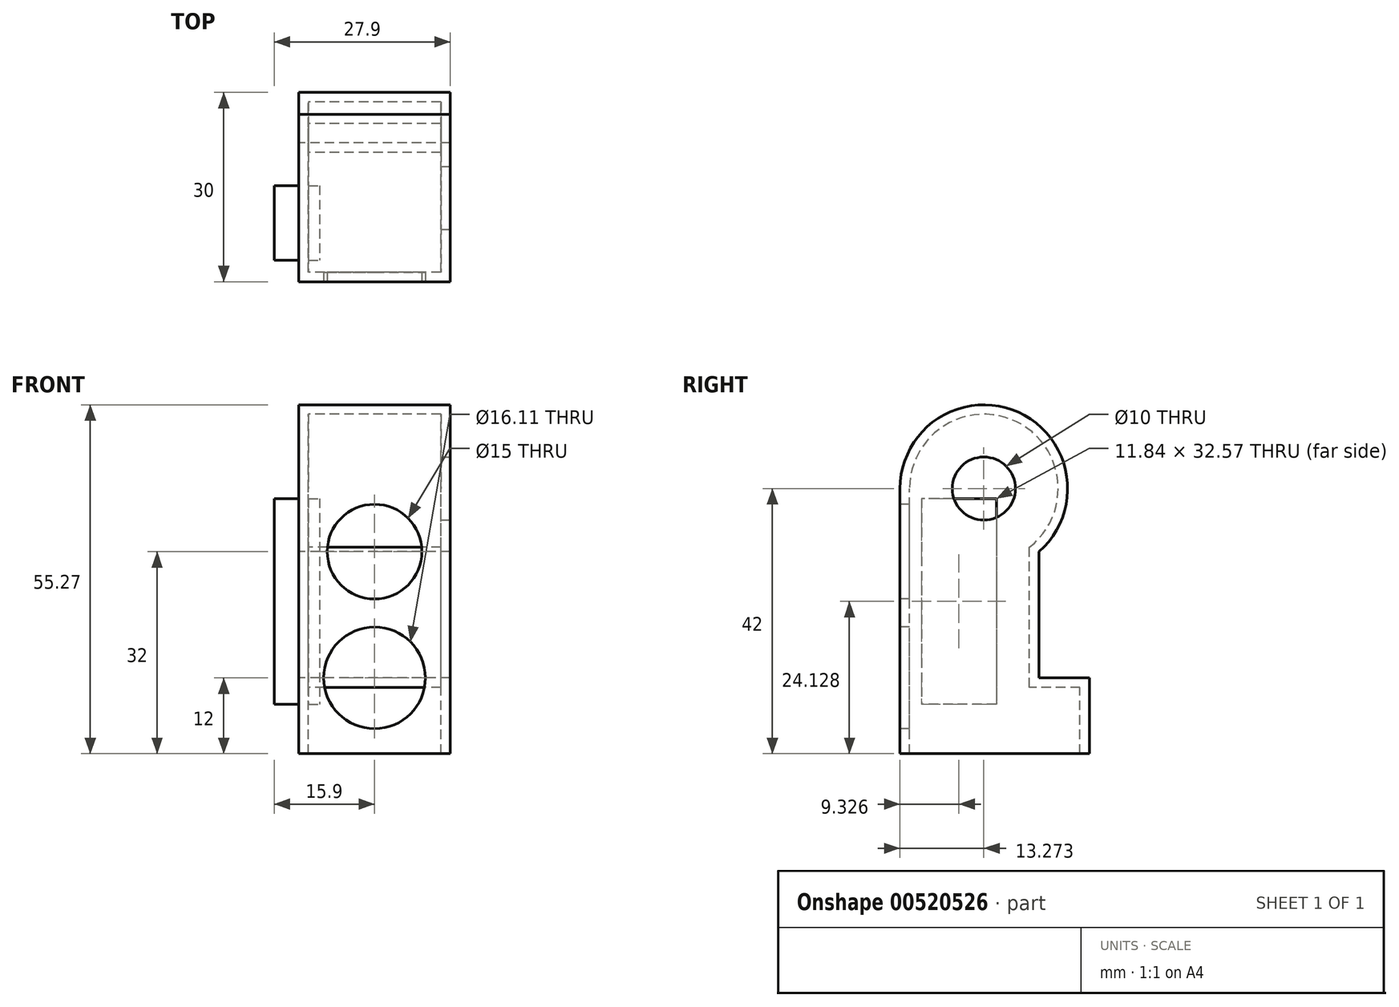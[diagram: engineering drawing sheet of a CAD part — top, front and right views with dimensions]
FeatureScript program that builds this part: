
annotation { "Feature Type Name" : "Feature", "Feature Type Description" : "" }
export const myFeature = defineFeature(function(context is Context, id is Id, definition is map)
    precondition{}
    {
        {
            var Q0;
            Q0=qCreatedBy(makeId("Right.planeOp"),FACE);
            var sketch = newSketch(context, id + "F0", { "sketchPlane" : qUnion([Q0])});
            skLineSegment(sketch, "E0", {"start": v(0, 0) * mm, "end": v(0, 42) * mm});
            skLineSegment(sketch, "E1", {"start": v(0, 0) * mm, "end": v(30, 0) * mm});
            skLineSegment(sketch, "E2", {"start": v(30, 0) * mm, "end": v(30, 12) * mm});
            skLineSegment(sketch, "E3", {"start": v(30, 12) * mm, "end": v(22, 12) * mm});
            skLineSegment(sketch, "E4", {"start": v(22, 12) * mm, "end": v(22, 32) * mm});
            skArc(sketch, "E5", {"start": v(22, 32) * mm, "mid": v(18.77, 54.08) * mm, "end": v(0, 42) * mm});
            skSolve(sketch);
        }
        {
            var Q0;
            Q0=makeQuery(id+"F0.imprint","IMPRINT",FACE,{"disambiguationData":[TD([[makeQuery(id+"F0.imprint","IMPRINT",EDGE,{"derivedFrom":sQuery(id+"F0.wireOp",EDGE,"E0")}),-1.0]])]});
            extrude(context, id + "F1", {"entities" : qUnion([Q0]), "endBound" : BoundingType.SYMMETRIC, "depth" : 24 * mm});
        }
        {
            var Q0;
            Q0=makeQuery(id+"F1.opExtrude","SWEPT_FACE",FACE,{"disambiguationData":[OSD([sQuery(id+"F0.wireOp",EDGE,"E1")])]});
            shell(context, id + "F2", {"entities" : qUnion([Q0]), "thickness" : 1.5 * mm});
        }
        {
            var Q0;
            Q0=makeQuery(id+"F1.opExtrude","CAP_FACE",FACE,{"disambiguationData":[OSD([sQuery(id+"F0.wireOp",EDGE,"E0"),sQuery(id+"F0.wireOp",EDGE,"E1"),sQuery(id+"F0.wireOp",EDGE,"E2"),sQuery(id+"F0.wireOp",EDGE,"E3"),sQuery(id+"F0.wireOp",EDGE,"E4"),sQuery(id+"F0.wireOp",EDGE,"E5")])],"isStart":false});
            var sketch = newSketch(context, id + "F3", { "sketchPlane" : qUnion([Q0])});
            skCircle(sketch, "E6", {"center": v(13.27, 42) * mm, "radius": 5 * mm});
            skSolve(sketch);
        }
        {
            var Q0;
            Q0=qSketchRegion(id+"F3",true);
            extrude(context, id + "F4", {"entities" : qUnion([Q0]), "operationType" : NewBodyOperationType.REMOVE, "oppositeDirection" : true, "depth" : 5 * mm});
        }
        {
            var Q0;
            Q0=makeQuery(id+"F1.opExtrude","SWEPT_FACE",FACE,{"disambiguationData":[OSD([sQuery(id+"F0.wireOp",EDGE,"E0")])]});
            var sketch = newSketch(context, id + "F5", { "sketchPlane" : qUnion([Q0])});
            skCircle(sketch, "E7", {"center": v(0, 12) * mm, "radius": 8.05 * mm});
            skCircle(sketch, "E8", {"center": v(0, 32) * mm, "radius": 7.5 * mm});
            skSolve(sketch);
        }
        {
            var Q0;
            Q0=makeQuery(id+"F5.imprint","IMPRINT",FACE,{"disambiguationData":[TD([[makeQuery(id+"F5.imprint","IMPRINT",EDGE,{"derivedFrom":sQuery(id+"F5.wireOp",EDGE,"E8")}),1.0]])]});
            var Q1;
            Q1=makeQuery(id+"F5.imprint","IMPRINT",FACE,{"disambiguationData":[TD([[makeQuery(id+"F5.imprint","IMPRINT",EDGE,{"derivedFrom":sQuery(id+"F5.wireOp",EDGE,"E7")}),1.0]])]});
            extrude(context, id + "F6", {"entities" : qUnion([Q0, Q1]), "operationType" : NewBodyOperationType.REMOVE, "oppositeDirection" : true, "depth" : 5 * mm});
        }
        {
            var Q0;
            Q0=makeQuery(id+"F1.opExtrude","SWEPT_BODY",BODY,{"disambiguationData":[OSD([sQuery(id+"F0.wireOp",EDGE,"E0"),sQuery(id+"F0.wireOp",EDGE,"E1"),sQuery(id+"F0.wireOp",EDGE,"E2"),sQuery(id+"F0.wireOp",EDGE,"E3"),sQuery(id+"F0.wireOp",EDGE,"E4"),sQuery(id+"F0.wireOp",EDGE,"E5")])]});
            var Q1;
            Q1=makeQuery(id+"F1.opExtrude","CAP_FACE",FACE,{"disambiguationData":[OSD([sQuery(id+"F0.wireOp",EDGE,"E0"),sQuery(id+"F0.wireOp",EDGE,"E1"),sQuery(id+"F0.wireOp",EDGE,"E2"),sQuery(id+"F0.wireOp",EDGE,"E3"),sQuery(id+"F0.wireOp",EDGE,"E4"),sQuery(id+"F0.wireOp",EDGE,"E5")])],"isStart":false});
            mirror(context, id + "F7", {"entities" : qUnion([Q0]), "mirrorPlane" : qUnion([Q1])});
        }
        {
            var Q0;
            Q0=makeQuery(id+"F7.opPattern","COPY",BODY,{"derivedFrom":makeQuery(id+"F1.opExtrude","SWEPT_BODY",BODY,{"disambiguationData":[OSD([sQuery(id+"F0.wireOp",EDGE,"E0"),sQuery(id+"F0.wireOp",EDGE,"E1"),sQuery(id+"F0.wireOp",EDGE,"E2"),sQuery(id+"F0.wireOp",EDGE,"E3"),sQuery(id+"F0.wireOp",EDGE,"E4"),sQuery(id+"F0.wireOp",EDGE,"E5")])]}),"instanceName":"1"});
            deleteBodies(context, id + "F8", {"entities" : qUnion([Q0])});
        }
        {
            var Q0;
            Q0=qCreatedBy(makeId("Right.planeOp"),FACE);
            var sketch = newSketch(context, id + "F9", { "sketchPlane" : qUnion([Q0])});
            skLineSegment(sketch, "E9.bottom", {"start": v(15.25, 40.41) * mm, "end": v(3.4, 40.41) * mm});
            skLineSegment(sketch, "E9.top", {"start": v(15.25, 7.85) * mm, "end": v(3.4, 7.85) * mm});
            skLineSegment(sketch, "E9.left", {"start": v(15.25, 40.41) * mm, "end": v(15.25, 7.85) * mm});
            skLineSegment(sketch, "E9.right", {"start": v(3.4, 40.41) * mm, "end": v(3.4, 7.85) * mm});
            skSolve(sketch);
        }
        {
            var Q0;
            Q0 = qSketchRegion(id + "F9", true);
            extrude(context, id + "F10", {"entities" : qUnion([Q0]), "operationType" : NewBodyOperationType.ADD, "oppositeDirection" : true, "depth" : 15.9 * mm, "offsetDistance" : 25 * mm, "hasSecondDirection" : true, "secondDirectionOppositeDirection" : true, "secondDirectionDepth" : 8.7 * mm});
        }
    });
